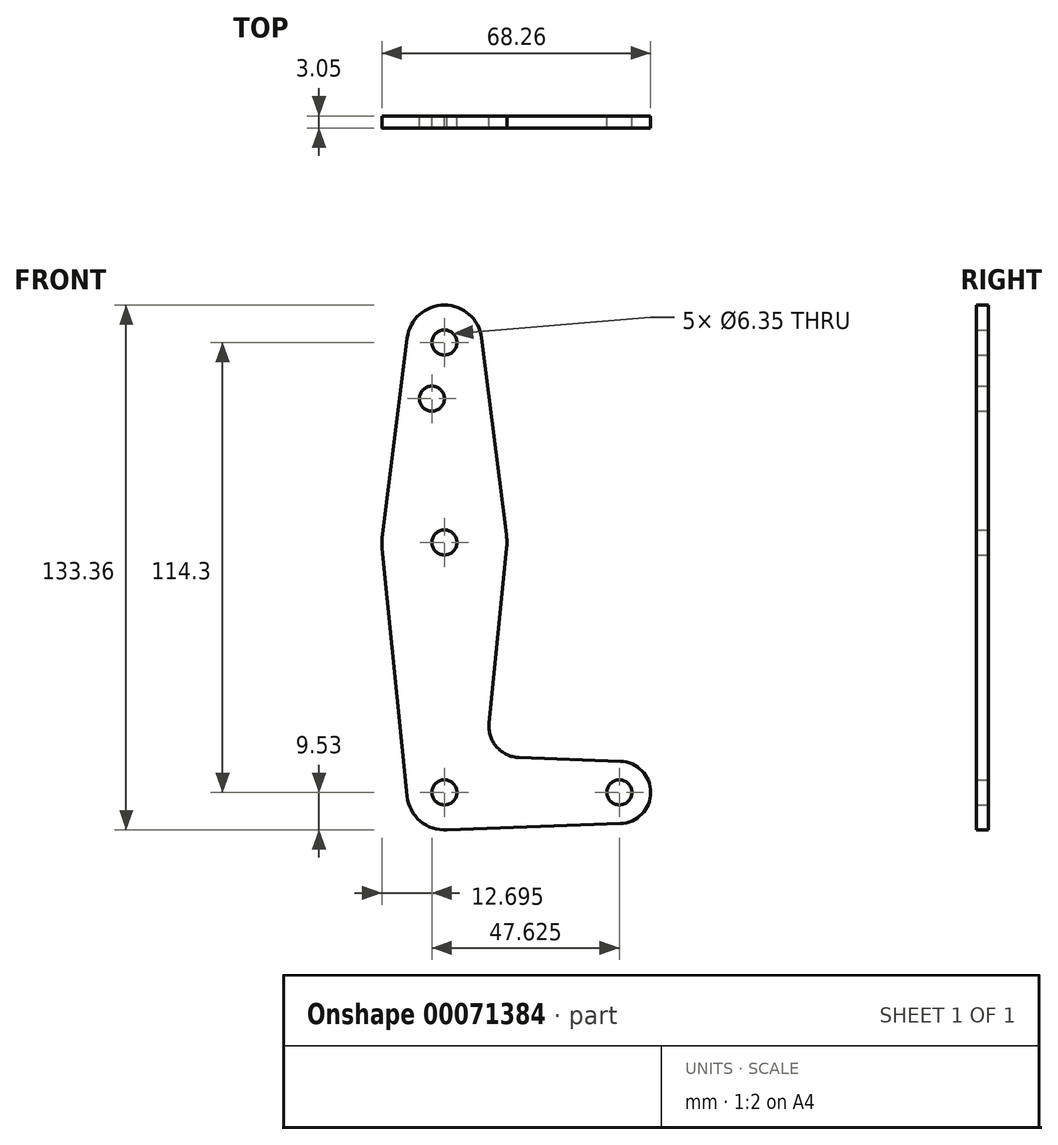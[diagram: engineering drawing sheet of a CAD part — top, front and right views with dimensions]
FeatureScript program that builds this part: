
annotation { "Feature Type Name" : "Feature", "Feature Type Description" : "" }
export const myFeature = defineFeature(function(context is Context, id is Id, definition is map)
    precondition{}
    {
        {
            var Q0;
            Q0=qCreatedBy(makeId("Front.planeOp"),FACE);
            var sketch = newSketch(context, id + "F0", { "sketchPlane" : qUnion([Q0])});
            skLineSegment(sketch, "E0", {"start": v(0, 0) * mm, "end": v(0, 63.5) * mm, "construction": true});
            skLineSegment(sketch, "E1", {"start": v(0, 63.5) * mm, "end": v(0, 114.3) * mm, "construction": true});
            skLineSegment(sketch, "E2", {"start": v(0, 0) * mm, "end": v(44.45, 0) * mm, "construction": true});
            skCircle(sketch, "E3", {"center": v(0, 114.3) * mm, "radius": 9.53 * mm});
            skCircle(sketch, "E4", {"center": v(0, 63.5) * mm, "radius": 15.88 * mm});
            skCircle(sketch, "E5", {"center": v(0, 0) * mm, "radius": 9.53 * mm});
            skCircle(sketch, "E6", {"center": v(44.45, 0) * mm, "radius": 7.94 * mm});
            skLineSegment(sketch, "E7", {"start": v(-9.45, 115.5) * mm, "end": v(-15.75, 65.48) * mm});
            skLineSegment(sketch, "E8", {"start": v(9.45, 115.5) * mm, "end": v(15.75, 65.48) * mm});
            skLineSegment(sketch, "E9", {"start": v(-9.48, -0.95) * mm, "end": v(-15.8, 61.91) * mm});
            skLineSegment(sketch, "E10", {"start": v(11.34, 17.6) * mm, "end": v(15.8, 61.91) * mm});
            skLineSegment(sketch, "E11", {"start": v(18.97, 8.85) * mm, "end": v(44.73, 7.93) * mm});
            skLineSegment(sketch, "E12", {"start": v(0, -9.53) * mm, "end": v(44.73, -7.93) * mm});
            skCircle(sketch, "E13", {"center": v(0, 114.3) * mm, "radius": 3.18 * mm});
            skCircle(sketch, "E14", {"center": v(0, 63.5) * mm, "radius": 3.18 * mm});
            skCircle(sketch, "E15", {"center": v(0, 0) * mm, "radius": 3.18 * mm});
            skCircle(sketch, "E16", {"center": v(44.45, 0) * mm, "radius": 3.18 * mm});
            skCircle(sketch, "E17", {"center": v(-3.18, 100.03) * mm, "radius": 3.18 * mm});
            skArc(sketch, "E18.filletArc", {"start": v(11.34, 17.6) * mm, "mid": v(13.26, 11.57) * mm, "end": v(18.97, 8.85) * mm});
            skLineSegment(sketch, "E19", {"start": v(18.97, 8.85) * mm, "end": v(0, 9.53) * mm, "construction": true});
            skSolve(sketch);
        }
        {
            var Q0;
            Q0 = qSketchRegion(id + "F0", true);
            extrude(context, id + "F1", {"entities" : qUnion([Q0]), "depth" : 3.05 * mm});
        }
    });
